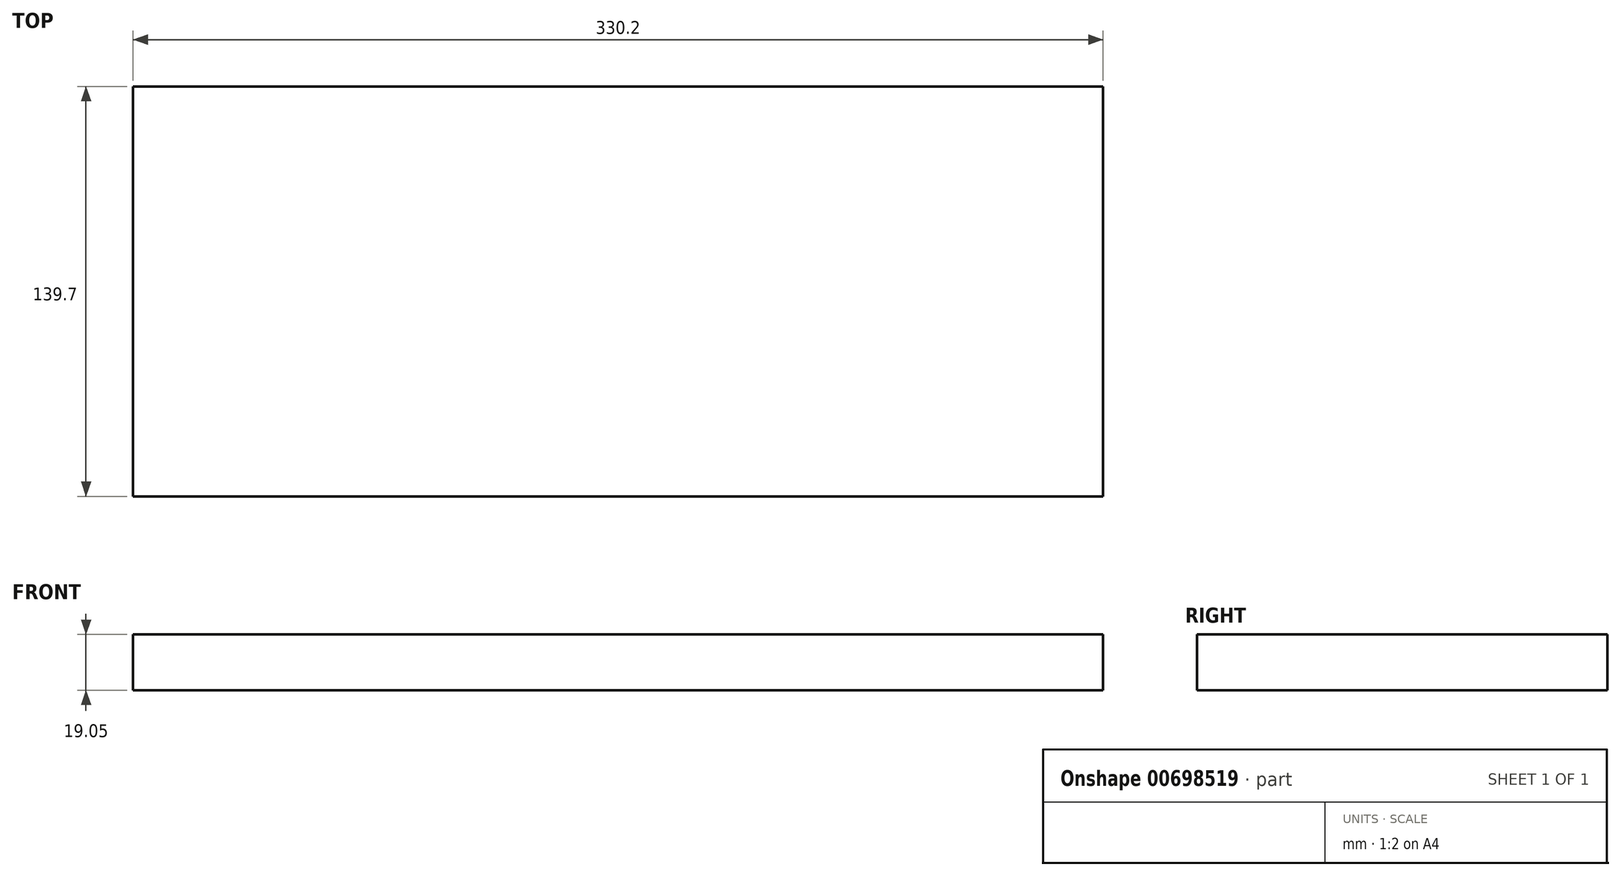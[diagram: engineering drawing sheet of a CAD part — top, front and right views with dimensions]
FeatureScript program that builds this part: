
annotation { "Feature Type Name" : "Feature", "Feature Type Description" : "" }
export const myFeature = defineFeature(function(context is Context, id is Id, definition is map)
    precondition{}
    {
        {
            var Q0;
            Q0=qCreatedBy(makeId("Top.planeOp"),FACE);
            var sketch = newSketch(context, id + "F0", { "sketchPlane" : qUnion([Q0])});
            skLineSegment(sketch, "E0.bottom", {"start": v(-169.74, -84.1) * mm, "end": v(160.46, -84.1) * mm});
            skLineSegment(sketch, "E0.top", {"start": v(-169.74, 55.6) * mm, "end": v(160.46, 55.6) * mm});
            skLineSegment(sketch, "E0.left", {"start": v(-169.74, -84.1) * mm, "end": v(-169.74, 55.6) * mm});
            skLineSegment(sketch, "E0.right", {"start": v(160.46, -84.1) * mm, "end": v(160.46, 55.6) * mm});
            skSolve(sketch);
        }
        {
            var Q0;
            Q0 = qSketchRegion(id + "F0", true);
            extrude(context, id + "F1", {"entities" : qUnion([Q0]), "depth" : 19.05 * mm, "offsetDistance" : 25.4 * mm});
        }
    });
